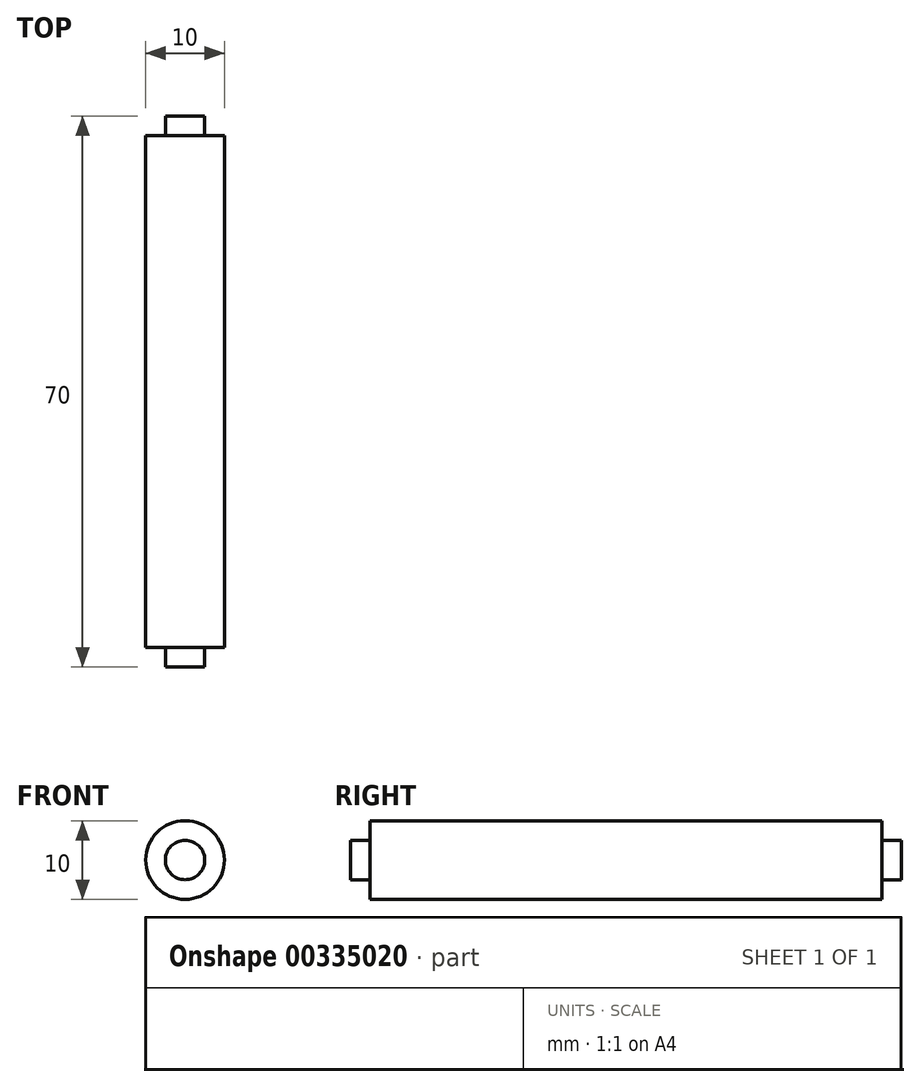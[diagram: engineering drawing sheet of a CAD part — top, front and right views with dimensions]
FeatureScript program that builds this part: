
annotation { "Feature Type Name" : "Feature", "Feature Type Description" : "" }
export const myFeature = defineFeature(function(context is Context, id is Id, definition is map)
    precondition{}
    {
        {
            var Q0;
            Q0=qCreatedBy(makeId("Front.planeOp"),FACE);
            var sketch = newSketch(context, id + "F0", { "sketchPlane" : qUnion([Q0])});
            skCircle(sketch, "E0", {"center": v(0, 0) * mm, "radius": 5 * mm});
            skSolve(sketch);
        }
        {
            var Q0;
            Q0=qSketchRegion(id+"F0",true);
            extrude(context, id + "F1", {"entities" : qUnion([Q0]), "depth" : 65 * mm});
        }
        {
            var Q0;
            Q0=makeQuery(id+"F1.opExtrude","CAP_FACE",FACE,{"disambiguationData":[OSD([sQuery(id+"F0.wireOp",EDGE,"E0")])],"isStart":false});
            var sketch = newSketch(context, id + "F2", { "sketchPlane" : qUnion([Q0])});
            skCircle(sketch, "E1", {"center": v(0, 0) * mm, "radius": 2.5 * mm});
            skSolve(sketch);
        }
        {
            var Q0;
            Q0=makeQuery(id+"F2.imprint","IMPRINT",FACE,{"disambiguationData":[TD([[makeQuery(id+"F2.imprint","IMPRINT",EDGE,{"derivedFrom":sQuery(id+"F2.wireOp",EDGE,"E1")}),1.0]])]});
            extrude(context, id + "F3", {"entities" : qUnion([Q0]), "operationType" : NewBodyOperationType.ADD, "depth" : 2.5 * mm, "hasSecondDirection" : true, "secondDirectionOppositeDirection" : true, "secondDirectionDepth" : 67.5 * mm});
        }
    });
